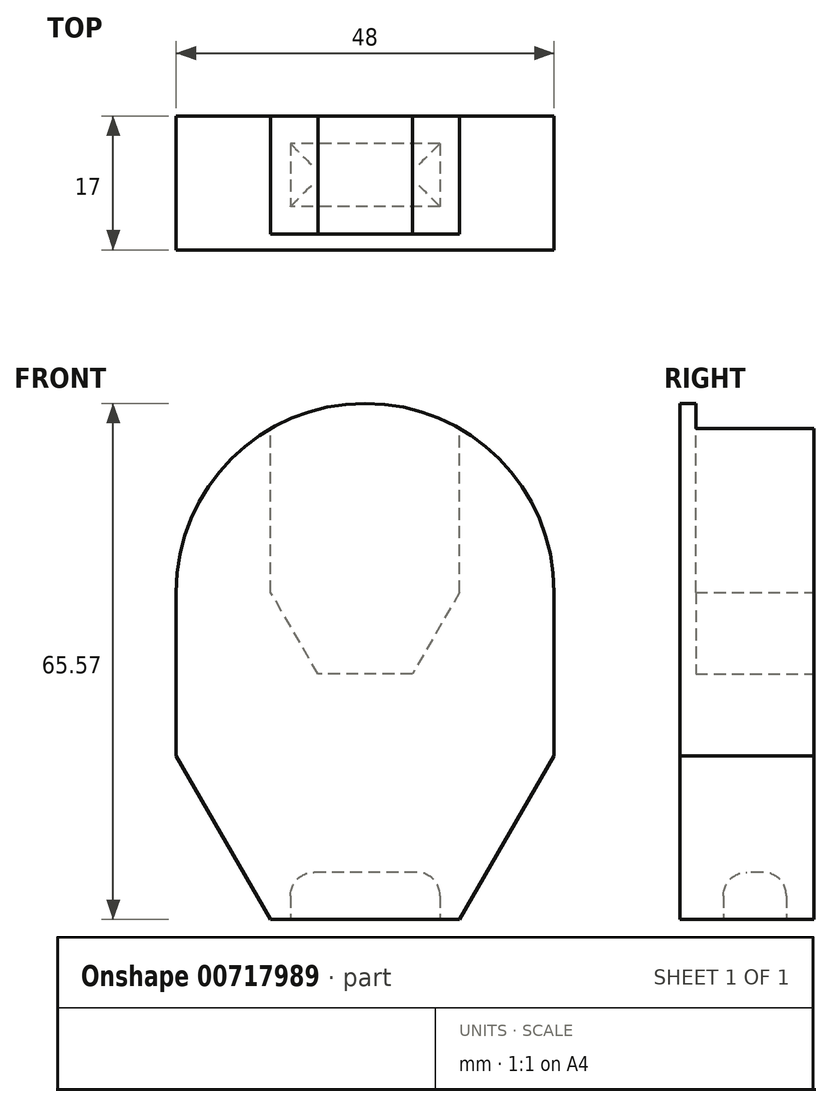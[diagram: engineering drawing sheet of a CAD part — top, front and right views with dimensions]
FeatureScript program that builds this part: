
annotation { "Feature Type Name" : "Feature", "Feature Type Description" : "" }
export const myFeature = defineFeature(function(context is Context, id is Id, definition is map)
    precondition{}
    {
        {
            var Q0;
            Q0=qCreatedBy(makeId("Front.planeOp"),FACE);
            var sketch = newSketch(context, id + "F0", { "sketchPlane" : qUnion([Q0])});
            skCircle(sketch, "E0.cCircle", {"center": v(0, 0) * mm, "radius": 24 * mm, "construction": true});
            skLineSegment(sketch, "E0.0", {"start": v(24, 0) * mm, "end": v(12, -20.78) * mm});
            skLineSegment(sketch, "E0.1", {"start": v(12, -20.78) * mm, "end": v(-12, -20.78) * mm});
            skLineSegment(sketch, "E0.2", {"start": v(-12, -20.78) * mm, "end": v(-24, 0) * mm});
            skLineSegment(sketch, "E0.3", {"start": v(-24, 0) * mm, "end": v(-12, 20.78) * mm});
            skLineSegment(sketch, "E0.4", {"start": v(-12, 20.78) * mm, "end": v(12, 20.78) * mm});
            skLineSegment(sketch, "E0.5", {"start": v(12, 20.78) * mm, "end": v(24, 0) * mm});
            skArc(sketch, "E1", {"start": v(24, 0) * mm, "mid": v(0, 24) * mm, "end": v(-24, 0) * mm});
            skCircle(sketch, "E2.cCircle", {"center": v(0, -20.78) * mm, "radius": 24 * mm, "construction": true});
            skPoint(sketch, "E2.cCircle.perimeterSnap0", {"position": v(0, -20.78) * mm});
            skLineSegment(sketch, "E2.0", {"start": v(24, -20.78) * mm, "end": v(12, -41.57) * mm});
            skPoint(sketch, "E2.0.startSnap0", {"position": v(0, -20.78) * mm});
            skLineSegment(sketch, "E2.1", {"start": v(12, -41.57) * mm, "end": v(-12, -41.57) * mm});
            skLineSegment(sketch, "E2.2", {"start": v(-12, -41.57) * mm, "end": v(-24, -20.78) * mm});
            skLineSegment(sketch, "E2.3", {"start": v(-24, -20.78) * mm, "end": v(-12, 0) * mm});
            skLineSegment(sketch, "E2.4", {"start": v(-12, 0) * mm, "end": v(12, 0) * mm});
            skLineSegment(sketch, "E2.5", {"start": v(12, 0) * mm, "end": v(24, -20.78) * mm});
            skLineSegment(sketch, "E3", {"start": v(-24, 0) * mm, "end": v(-24, -20.78) * mm});
            skLineSegment(sketch, "E4", {"start": v(24, 0) * mm, "end": v(24, -20.78) * mm});
            skCircle(sketch, "E5.cCircle", {"center": v(0, 0) * mm, "radius": 12 * mm, "construction": true});
            skLineSegment(sketch, "E5.0", {"start": v(12, 0) * mm, "end": v(6, -10.4) * mm});
            skLineSegment(sketch, "E5.1", {"start": v(6, -10.4) * mm, "end": v(-6, -10.4) * mm});
            skLineSegment(sketch, "E5.2", {"start": v(-6, -10.4) * mm, "end": v(-12, 0) * mm});
            skLineSegment(sketch, "E5.3", {"start": v(-12, 0) * mm, "end": v(-6, 10.4) * mm});
            skLineSegment(sketch, "E5.4", {"start": v(-6, 10.4) * mm, "end": v(6, 10.4) * mm});
            skLineSegment(sketch, "E5.5", {"start": v(6, 10.4) * mm, "end": v(12, 0) * mm});
            skLineSegment(sketch, "E6", {"start": v(-12, 0) * mm, "end": v(-12, 20.78) * mm});
            skLineSegment(sketch, "E7", {"start": v(12, 0) * mm, "end": v(12, 20.78) * mm});
            skSolve(sketch);
        }
        {
            var Q0;
            {var subQ1=sQuery(id+"F0.wireOp",EDGE,"E0.1");Q0=makeQuery(id+"F0.imprint","IMPRINT",FACE,{"disambiguationData":[TD([[makeQuery(id+"F0.imprint","IMPRINT",EDGE,{"derivedFrom":subQ1}),1.0]])]});}
            var Q1;
            {var subQ5=sQuery(id+"F0.wireOp",EDGE,"E0.1");Q1=makeQuery(id+"F0.imprint","IMPRINT",FACE,{"disambiguationData":[TD([[makeQuery(id+"F0.imprint","IMPRINT",EDGE,{"derivedFrom":subQ5}),-1.0]])]});}
            var Q2;
            {var subQ0=sQuery(id+"F0.wireOp",EDGE,"E0.3");Q2=makeQuery(id+"F0.imprint","IMPRINT",FACE,{"disambiguationData":[TD([[makeQuery(id+"F0.imprint","IMPRINT",EDGE,{"derivedFrom":subQ0}),-1.0]])]});}
            var Q3;
            {var subQ0=sQuery(id+"F0.wireOp",EDGE,"E0.5");Q3=makeQuery(id+"F0.imprint","IMPRINT",FACE,{"disambiguationData":[TD([[makeQuery(id+"F0.imprint","IMPRINT",EDGE,{"derivedFrom":subQ0}),-1.0]])]});}
            var Q4;
            {var subQ0=sQuery(id+"F0.wireOp",EDGE,"E0.3");Q4=makeQuery(id+"F0.imprint","IMPRINT",FACE,{"disambiguationData":[TD([[makeQuery(id+"F0.imprint","IMPRINT",EDGE,{"derivedFrom":subQ0}),1.0]])]});}
            var Q5;
            {var subQ0=sQuery(id+"F0.wireOp",EDGE,"E0.5");Q5=makeQuery(id+"F0.imprint","IMPRINT",FACE,{"disambiguationData":[TD([[makeQuery(id+"F0.imprint","IMPRINT",EDGE,{"derivedFrom":subQ0}),1.0]])]});}
            var Q6;
            {var subQ0=sQuery(id+"F0.wireOp",EDGE,"E4");Q6=makeQuery(id+"F0.imprint","IMPRINT",FACE,{"disambiguationData":[TD([[makeQuery(id+"F0.imprint","IMPRINT",EDGE,{"derivedFrom":subQ0}),-1.0]])]});}
            var Q7;
            {var subQ0=sQuery(id+"F0.wireOp",EDGE,"E3");Q7=makeQuery(id+"F0.imprint","IMPRINT",FACE,{"disambiguationData":[TD([[makeQuery(id+"F0.imprint","IMPRINT",EDGE,{"derivedFrom":subQ0}),1.0]])]});}
            extrude(context, id + "F1", {"entities" : qUnion([Q0, Q1, Q2, Q3, Q4, Q5, Q6, Q7]), "depth" : 15 * mm, "offsetDistance" : 25 * mm});
        }
        {
            var Q0;
            Q0=makeQuery(id+"F1.opExtrude","SWEPT_FACE",FACE,{"disambiguationData":[OSD([sQuery(id+"F0.wireOp",EDGE,"E2.1")])]});
            var sketch = newSketch(context, id + "F2", { "sketchPlane" : qUnion([Q0])});
            skLineSegment(sketch, "E8.bottom", {"start": v(9.5, 3.5) * mm, "end": v(-9.5, 3.5) * mm});
            skLineSegment(sketch, "E8.top", {"start": v(9.5, 11.5) * mm, "end": v(-9.5, 11.5) * mm});
            skLineSegment(sketch, "E8.left", {"start": v(9.5, 3.5) * mm, "end": v(9.5, 11.5) * mm});
            skLineSegment(sketch, "E8.right", {"start": v(-9.5, 3.5) * mm, "end": v(-9.5, 11.5) * mm});
            skPoint(sketch, "E8.middle", {"position": v(0, 7.5) * mm});
            skPoint(sketch, "E8.middle.positionSnap0", {"position": v(-12, 7.5) * mm});
            skPoint(sketch, "E8.centerSnap0", {"position": v(-12, 7.5) * mm});
            skSolve(sketch);
        }
        {
            var Q0;
            Q0 = qSketchRegion(id + "F2", true);
            extrude(context, id + "F3", {"entities" : qUnion([Q0]), "operationType" : NewBodyOperationType.REMOVE, "oppositeDirection" : true, "depth" : 6 * mm, "offsetDistance" : 25 * mm});
        }
        {
            var Q0;
            Q0=makeQuery(id+"F1.opExtrude","CAP_FACE",FACE,{"disambiguationData":[OSD([sQuery(id+"F0.wireOp",EDGE,"E1"),sQuery(id+"F0.wireOp",EDGE,"E2.0"),sQuery(id+"F0.wireOp",EDGE,"E2.1"),sQuery(id+"F0.wireOp",EDGE,"E2.2"),sQuery(id+"F0.wireOp",EDGE,"E3"),sQuery(id+"F0.wireOp",EDGE,"E4"),sQuery(id+"F0.wireOp",EDGE,"E5.0"),sQuery(id+"F0.wireOp",EDGE,"E5.1"),sQuery(id+"F0.wireOp",EDGE,"E5.2"),sQuery(id+"F0.wireOp",EDGE,"E6"),sQuery(id+"F0.wireOp",EDGE,"E7")])],"isStart":false});
            var sketch = newSketch(context, id + "F4", { "sketchPlane" : qUnion([Q0])});
            skCircle(sketch, "E9", {"center": v(0, 0) * mm, "radius": 24 * mm});
            skLineSegment(sketch, "E10", {"start": v(-24, 0) * mm, "end": v(-24, -20.78) * mm});
            skLineSegment(sketch, "E11", {"start": v(-24, -20.78) * mm, "end": v(-12, -41.57) * mm});
            skLineSegment(sketch, "E12", {"start": v(-12, -41.57) * mm, "end": v(12, -41.57) * mm});
            skLineSegment(sketch, "E13", {"start": v(12, -41.57) * mm, "end": v(24, -20.78) * mm});
            skLineSegment(sketch, "E14", {"start": v(24, -20.78) * mm, "end": v(24, 0) * mm});
            skSolve(sketch);
        }
        {
            var Q0;
            Q0 = qSketchRegion(id + "F4", true);
            extrude(context, id + "F5", {"entities" : qUnion([Q0]), "operationType" : NewBodyOperationType.ADD, "depth" : 2 * mm, "offsetDistance" : 25 * mm});
        }
        {
            var Q0;
            Q0=makeQuery(id+"F3.boolean.opBoolean","COPY",EDGE,{"derivedFrom":makeQuery(id+"F3.opExtrude","CAP_EDGE",EDGE,{"disambiguationData":[OSD([sQuery(id+"F2.wireOp",EDGE,"E8.bottom")])],"isStart":false})});
            var Q1;
            Q1=makeQuery(id+"F3.boolean.opBoolean","COPY",EDGE,{"derivedFrom":makeQuery(id+"F3.opExtrude","CAP_EDGE",EDGE,{"disambiguationData":[OSD([sQuery(id+"F2.wireOp",EDGE,"E8.right")])],"isStart":false})});
            var Q2;
            Q2=makeQuery(id+"F3.boolean.opBoolean","COPY",EDGE,{"derivedFrom":makeQuery(id+"F3.opExtrude","CAP_EDGE",EDGE,{"disambiguationData":[OSD([sQuery(id+"F2.wireOp",EDGE,"E8.top")])],"isStart":false})});
            var Q3;
            Q3=makeQuery(id+"F3.boolean.opBoolean","COPY",EDGE,{"derivedFrom":makeQuery(id+"F3.opExtrude","CAP_EDGE",EDGE,{"disambiguationData":[OSD([sQuery(id+"F2.wireOp",EDGE,"E8.left")])],"isStart":false})});
            fillet(context, id + "F6", {"entities" : qUnion([Q0, Q1, Q2, Q3]), "radius" : 3 * mm, "tangentPropagation" : true, "allowEdgeOverflow" : false});
        }
    });
